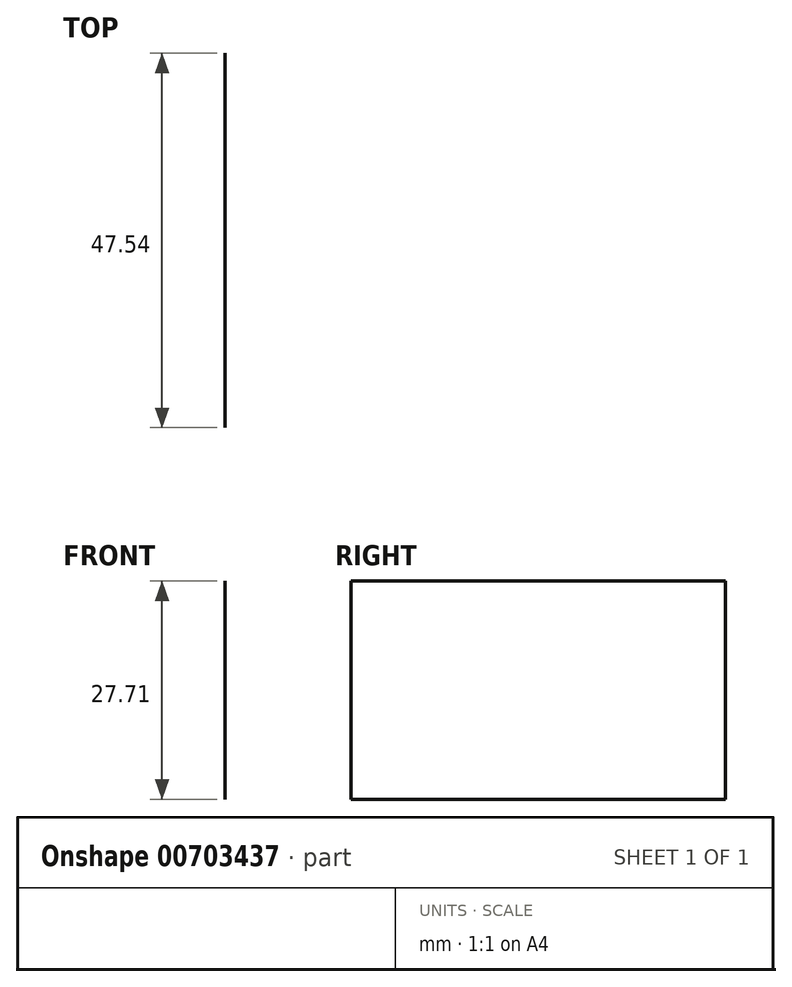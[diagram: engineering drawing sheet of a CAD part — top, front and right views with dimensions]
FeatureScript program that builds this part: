
annotation { "Feature Type Name" : "Feature", "Feature Type Description" : "" }
export const myFeature = defineFeature(function(context is Context, id is Id, definition is map)
    precondition{}
    {
        {
            var Q0;
            Q0=qCreatedBy(makeId("Front.planeOp"),FACE);
            var sketch = newSketch(context, id + "F0", { "sketchPlane" : qUnion([Q0])});
            skLineSegment(sketch, "E0.bottom", {"start": v(72.85, 37.75) * mm, "end": v(-72.85, 37.75) * mm});
            skLineSegment(sketch, "E0.top", {"start": v(72.85, 10.04) * mm, "end": v(-72.85, 10.04) * mm});
            skLineSegment(sketch, "E0.left", {"start": v(72.85, 37.75) * mm, "end": v(72.85, 10.04) * mm});
            skLineSegment(sketch, "E0.right", {"start": v(-72.85, 37.75) * mm, "end": v(-72.85, 10.04) * mm});
            skPoint(sketch, "E0.middle", {"position": v(0, 23.9) * mm});
            skSolve(sketch);
        }
        {
            var Q0;
            Q0=sQuery(id+"F0.wireOp",EDGE,"E0.left");
            extrude(context, id + "F1", {"bodyType" : ToolBodyType.SURFACE, "surfaceEntities" : qUnion([Q0]), "oppositeDirection" : true, "depth" : 47.54 * mm, "offsetDistance" : 25.4 * mm});
        }
    });
